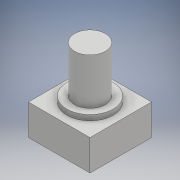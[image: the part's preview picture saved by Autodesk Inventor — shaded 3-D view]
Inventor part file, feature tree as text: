
AUTODESK INVENTOR PART (.ipt)
format: ipt  version: 2017 (Build 210142000, 142)  size: 231,936 bytes
history: native  units: mm
features: extrude x3, sketch x3
ambient origin geometry x8: Origin, YZ Plane, XZ Plane, XY Plane, X Axis, Y Axis, Z Axis, Center Point
bodies: Solid1 (feature_tree)
feature tree (6):
  extrude  "Extrusion1"  Depth=4.0mm TaperAngle=0.0deg
  extrude  "Extrusion2"  Depth=0.7mm TaperAngle=0.0deg
  extrude  "Extrusion3"  Depth=6.0mm TaperAngle=0.0deg
  sketch  "Sketch1"  dims[d0=8.0mm d1=4.0mm d2=0.0mm]
  sketch  "Sketch2"  dims[d3=6.0mm d4=0.7mm d5=0.0mm]
  sketch  "Sketch3"  dims[d6=4.0mm d7=6.0mm d8=0.0mm]
